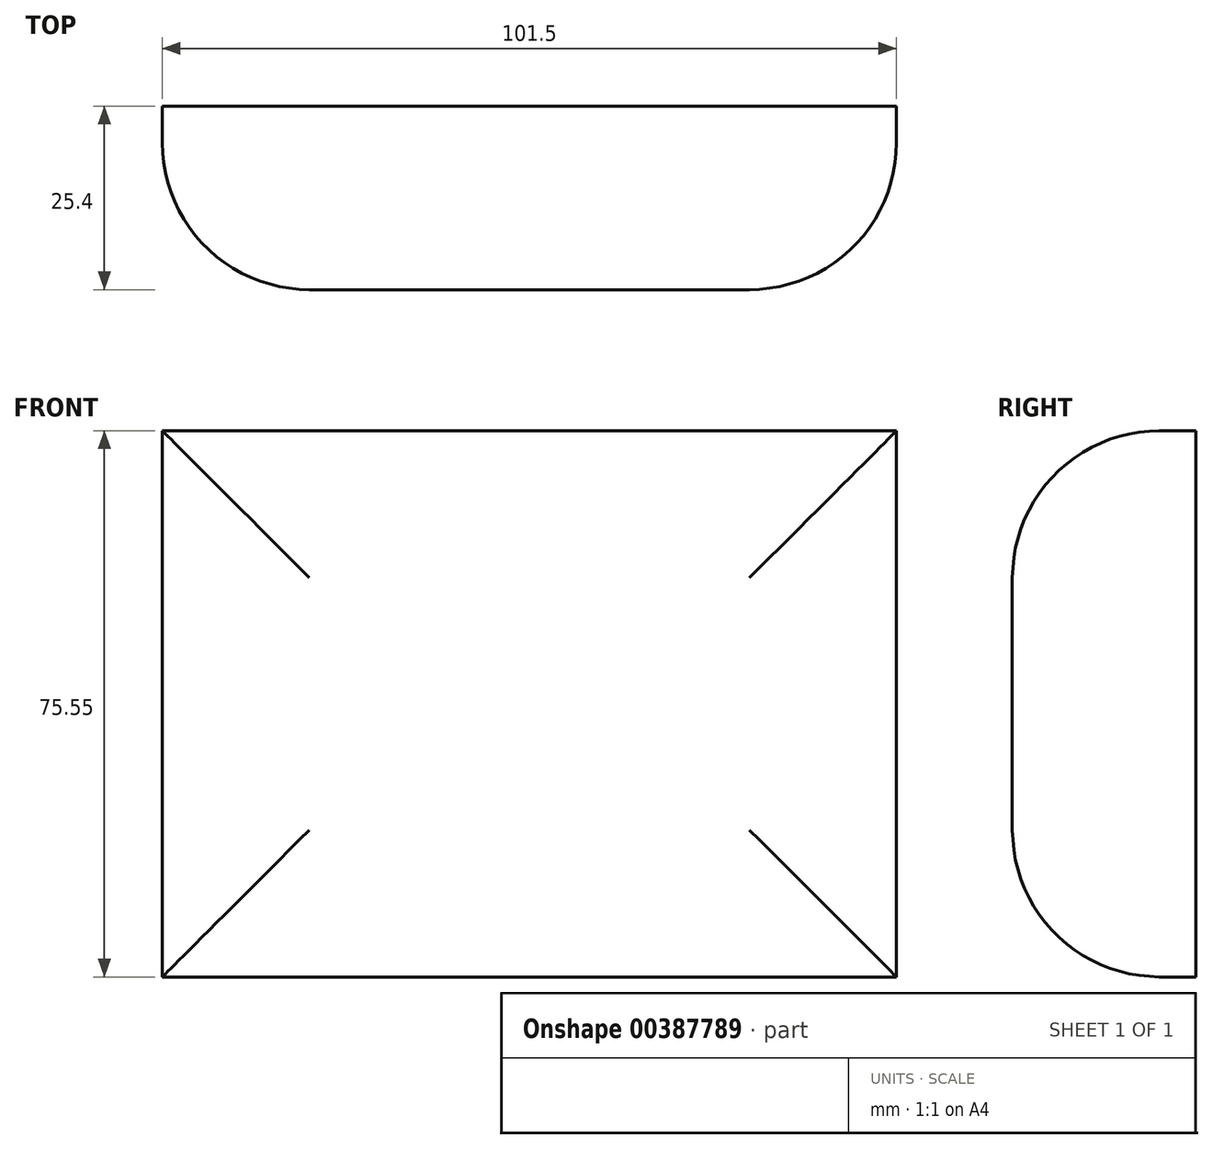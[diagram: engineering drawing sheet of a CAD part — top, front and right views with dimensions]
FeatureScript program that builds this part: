
annotation { "Feature Type Name" : "Feature", "Feature Type Description" : "" }
export const myFeature = defineFeature(function(context is Context, id is Id, definition is map)
    precondition{}
    {
        {
            var Q0;
            Q0=qCreatedBy(makeId("Front.planeOp"),FACE);
            var sketch = newSketch(context, id + "F0", { "sketchPlane" : qUnion([Q0])});
            skLineSegment(sketch, "E0.bottom", {"start": v(0, 0) * mm, "end": v(-101.5, 0) * mm});
            skLineSegment(sketch, "E0.top", {"start": v(0, 75.55) * mm, "end": v(-101.5, 75.55) * mm});
            skLineSegment(sketch, "E0.left", {"start": v(0, 0) * mm, "end": v(0, 75.55) * mm});
            skLineSegment(sketch, "E0.right", {"start": v(-101.5, 0) * mm, "end": v(-101.5, 75.55) * mm});
            skPoint(sketch, "E0.middle", {"position": v(-50.75, 37.78) * mm});
            skSolve(sketch);
        }
        {
            var Q0;
            Q0 = qSketchRegion(id + "F0", true);
            extrude(context, id + "F1", {"entities" : qUnion([Q0]), "depth" : 25.4 * mm});
        }
        {
            var Q0;
            Q0=makeQuery(id+"F1.opExtrude","CAP_EDGE",EDGE,{"disambiguationData":[OSD([sQuery(id+"F0.wireOp",EDGE,"E0.bottom")])],"isStart":false});
            var Q1;
            Q1=makeQuery(id+"F1.opExtrude","CAP_EDGE",EDGE,{"disambiguationData":[OSD([sQuery(id+"F0.wireOp",EDGE,"E0.right")])],"isStart":false});
            var Q2;
            Q2=makeQuery(id+"F1.opExtrude","CAP_FACE",FACE,{"disambiguationData":[OSD([sQuery(id+"F0.wireOp",EDGE,"E0.bottom"),sQuery(id+"F0.wireOp",EDGE,"E0.top"),sQuery(id+"F0.wireOp",EDGE,"E0.left"),sQuery(id+"F0.wireOp",EDGE,"E0.right")])],"isStart":false});
            var Q3;
            Q3=makeQuery(id+"F1.opExtrude","CAP_EDGE",EDGE,{"disambiguationData":[OSD([sQuery(id+"F0.wireOp",EDGE,"E0.top")])],"isStart":false});
            fillet(context, id + "F2", {"entities" : qUnion([Q0, Q1, Q2, Q3]), "radius" : 20.32 * mm, "tangentPropagation" : true, "allowEdgeOverflow" : false});
        }
    });
